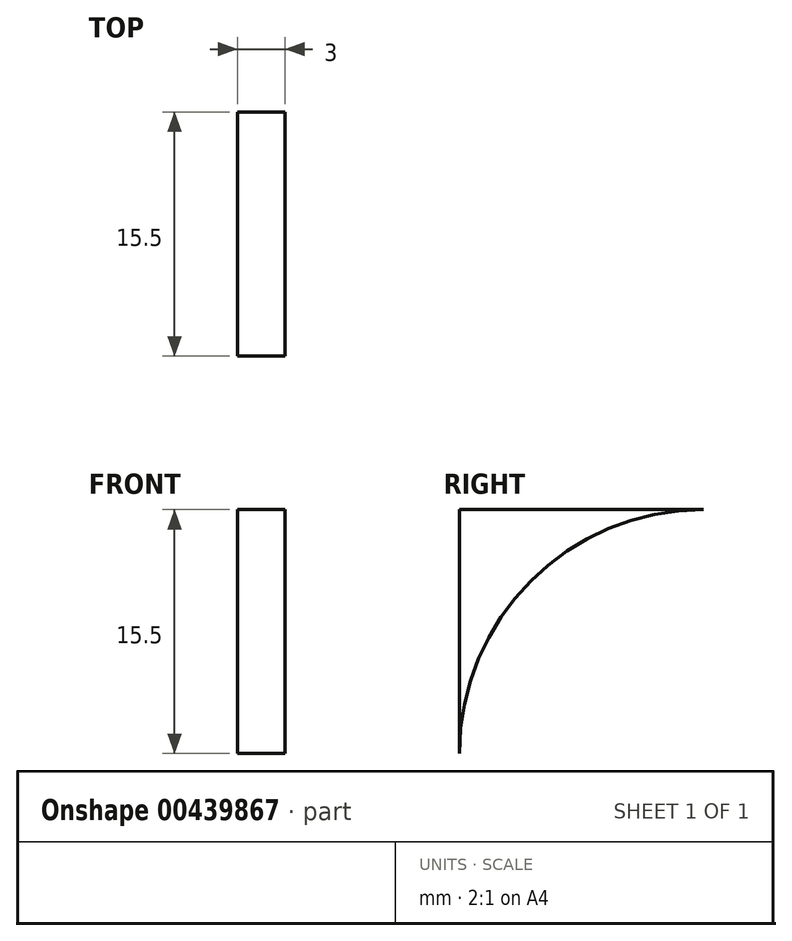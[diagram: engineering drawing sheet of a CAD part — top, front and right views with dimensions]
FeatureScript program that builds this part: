
annotation { "Feature Type Name" : "Feature", "Feature Type Description" : "" }
export const myFeature = defineFeature(function(context is Context, id is Id, definition is map)
    precondition{}
    {
        {
            assignVariable(context, id + "F0", {"name" : "x3", "anyValue" : 315});
        }
        {
            assignVariable(context, id + "F1", {"name" : "x4", "anyValue" : 15});
        }
        {
            assignVariable(context, id + "F2", {"name" : "x5", "anyValue" : 60});
        }
        {
            var Q0;
            Q0=qCreatedBy(makeId("Front.planeOp"),FACE);
            var sketch = newSketch(context, id + "F3", { "sketchPlane" : qUnion([Q0])});
            skLineSegment(sketch, "E0", {"start": v(0, 0) * mm, "end": v(0, 31) * mm});
            skLineSegment(sketch, "E1", {"start": v(0, 31) * mm, "end": v(-3, 31) * mm});
            skLineSegment(sketch, "E2", {"start": v(-3, 31) * mm, "end": v(-3, 3) * mm});
            skLineSegment(sketch, "E3", {"start": v(-3, 3) * mm, "end": v(-31, 3) * mm});
            skLineSegment(sketch, "E4", {"start": v(-31, 3) * mm, "end": v(-31, 0) * mm});
            skLineSegment(sketch, "E5", {"start": v(-31, 0) * mm, "end": v(0, 0) * mm});
            skSolve(sketch);
        }
        {
            var Q0;
            Q0=makeQuery(id+"F3.imprint","IMPRINT",FACE,{"disambiguationData":[TD([[makeQuery(id+"F3.imprint","IMPRINT",EDGE,{"derivedFrom":sQuery(id+"F3.wireOp",EDGE,"E0")}),1.0]])]});
            extrude(context, id + "F4", {"entities" : qUnion([Q0]), "depth" : (getVariable(context, 'x3') - getVariable(context, 'x4') + (getVariable(context, 'x5') - 2)) * mm});
        }
        {
            var Q0;
            Q0=makeQuery(id+"F4.opExtrude","SWEPT_FACE",FACE,{"disambiguationData":[OSD([sQuery(id+"F3.wireOp",EDGE,"E0")])]});
            var sketch = newSketch(context, id + "F5", { "sketchPlane" : qUnion([Q0])});
            skCircle(sketch, "E6", {"center": v(-21.5, 15.5) * mm, "radius": 4.5 * mm});
            skCircle(sketch, "E7", {"center": v(-330, 15.5) * mm, "radius": 4.5 * mm});
            skPoint(sketch, "E7.centerSnap0", {"position": v(-358, 15.5) * mm});
            skCircle(sketch, "E8", {"center": v(-45, 15.5) * mm, "radius": 4.5 * mm});
            skLineSegment(sketch, "E9", {"start": v(-330, 20) * mm, "end": v(-45, 20) * mm});
            skLineSegment(sketch, "E10", {"start": v(-330, 11) * mm, "end": v(-45, 11) * mm});
            skPoint(sketch, "E11", {"position": v(-342.5, 15.5) * mm});
            skArc(sketch, "E12", {"start": v(-358, 15.5) * mm, "mid": v(-353.46, 26.46) * mm, "end": v(-342.5, 31) * mm});
            skSolve(sketch);
        }
        {
            var Q0;
            Q0=makeQuery(id+"F5.imprint","IMPRINT",FACE,{"disambiguationData":[TD([[makeQuery(id+"F5.imprint","IMPRINT",EDGE,{"derivedFrom":sQuery(id+"F5.wireOp",EDGE,"E7")}),1.0]])]});
            var Q1;
            Q1=makeQuery(id+"F5.imprint","IMPRINT",FACE,{"disambiguationData":[TD([[makeQuery(id+"F5.imprint","IMPRINT",EDGE,{"derivedFrom":sQuery(id+"F5.wireOp",EDGE,"E6")}),1.0]])]});
            var Q2;
            {var subQ0=sQuery(id+"F5.wireOp",EDGE,"E9");Q2=makeQuery(id+"F5.imprint","IMPRINT",FACE,{"disambiguationData":[TD([[makeQuery(id+"F5.imprint","IMPRINT",EDGE,{"derivedFrom":subQ0}),-1.0]])]});}
            var Q3;
            {var subQ0=sQuery(id+"F5.wireOp",EDGE,"E8");var subQ1=makeQuery(id+"F5.imprint","INTERSECT",VERTEX,{"derivedFrom":[subQ0,sQuery(id+"F5.wireOp",EDGE,"E9")]});Q3=makeQuery(id+"F5.imprint","IMPRINT",FACE,{"disambiguationData":[TD([[makeQuery(id+"F5.imprint","IMPRINT",EDGE,{"disambiguationData":[TD([[subQ1,-1.0]])],"derivedFrom":subQ0}),1.0]])]});}
            var Q4;
            {var subQ0=sQuery(id+"F5.wireOp",EDGE,"E12");Q4=makeQuery(id+"F5.imprint","IMPRINT",FACE,{"disambiguationData":[TD([[makeQuery(id+"F5.imprint","IMPRINT",EDGE,{"derivedFrom":subQ0}),1.0]])]});}
            extrude(context, id + "F6", {"entities" : qUnion([Q0, Q1, Q2, Q3, Q4]), "operationType" : NewBodyOperationType.REMOVE, "endBound" : BoundingType.UP_TO_NEXT, "oppositeDirection" : true, "depth" : 25 * mm});
        }
    });
